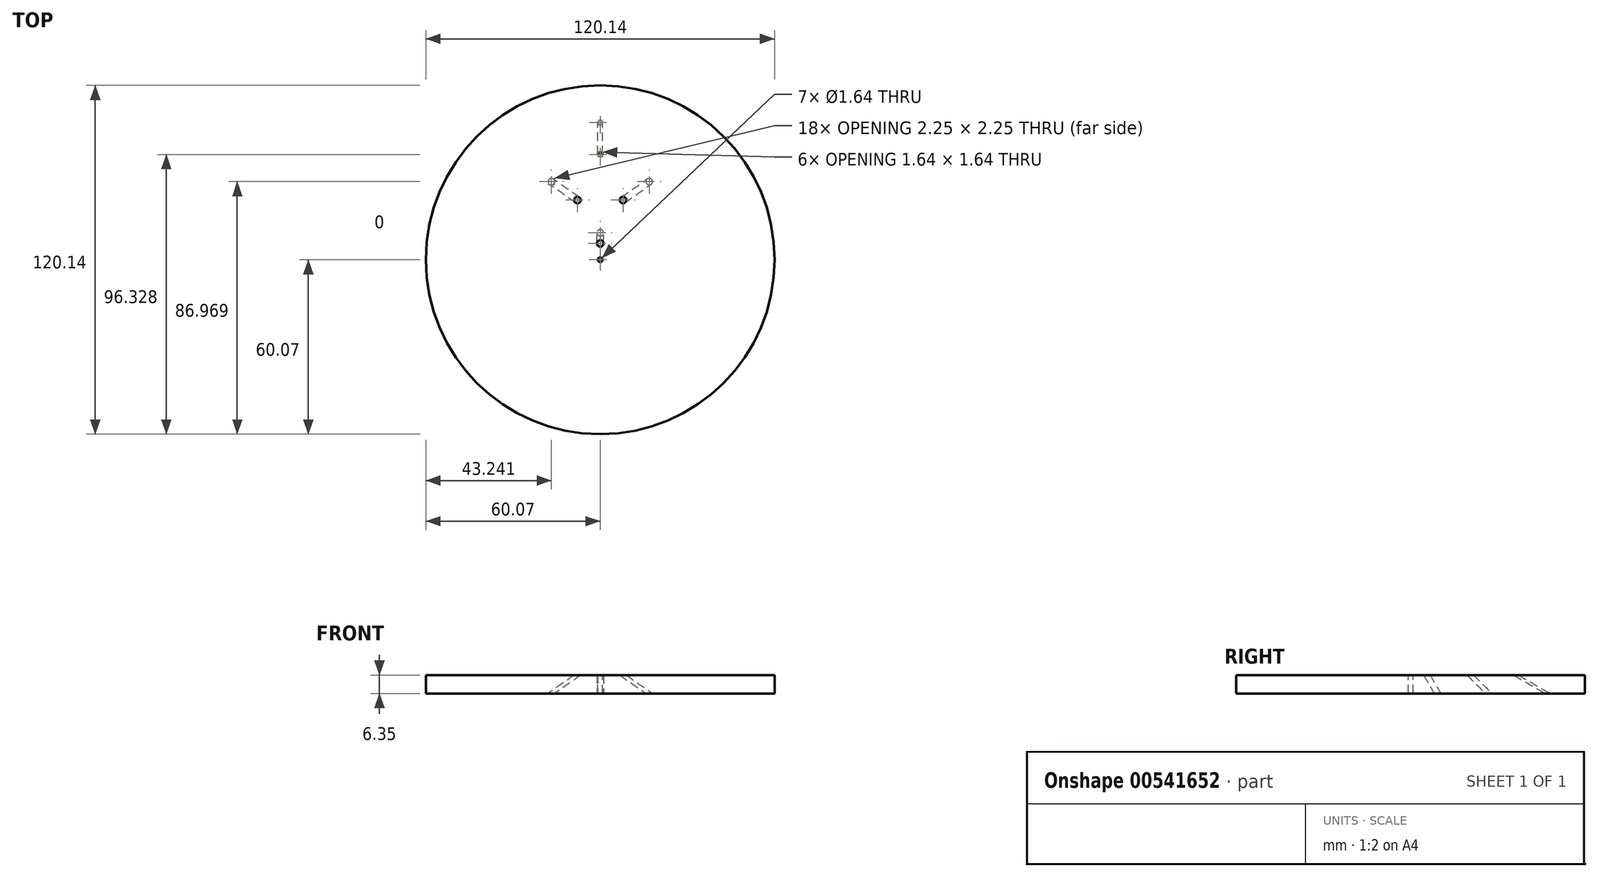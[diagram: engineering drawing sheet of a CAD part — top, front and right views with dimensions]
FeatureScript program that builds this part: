
annotation { "Feature Type Name" : "Feature", "Feature Type Description" : "" }
export const myFeature = defineFeature(function(context is Context, id is Id, definition is map)
    precondition{}
    {
        {
            var Q0;
            Q0=qCreatedBy(makeId("Top.planeOp"),FACE);
            var sketch = newSketch(context, id + "F0", { "sketchPlane" : qUnion([Q0])});
            skCircle(sketch, "E0", {"center": v(0, 0) * mm, "radius": 60.07 * mm});
            skSolve(sketch);
        }
        {
            var Q0;
            Q0=qCreatedBy(makeId("Top.planeOp"),FACE);
            var sketch = newSketch(context, id + "F1", { "sketchPlane" : qUnion([Q0])});
            skCircle(sketch, "E1", {"center": v(0, 0) * mm, "radius": 0.82 * mm});
            skCircle(sketch, "E2", {"center": v(0, 5.61) * mm, "radius": 1.12 * mm});
            skCircle(sketch, "E3", {"center": v(0, 36.26) * mm, "radius": 0.82 * mm});
            skCircle(sketch, "E4", {"center": v(-7.85, 20.55) * mm, "radius": 1.12 * mm});
            skCircle(sketch, "E5", {"center": v(7.85, 20.55) * mm, "radius": 1.12 * mm});
            skLineSegment(sketch, "E6", {"start": v(7.85, 20.55) * mm, "end": v(-7.85, 20.55) * mm, "construction": true});
            skSolve(sketch);
        }
        {
            var Q0;
            Q0=sQuery(id+"F1.wireOp",EDGE,"E6");
            cPlane(context, id + "F2", {"entities" : qUnion([Q0]), "cplaneType" : CPlaneType.LINE_ANGLE, "offset" : 25.4 * mm, "angle" : 45 * degree, "oppositeDirection" : true, "width" : 152.4 * mm, "height" : 152.4 * mm});
        }
        {
            var Q0;
            Q0=qCreatedBy(makeId("Top.planeOp"),FACE);
            var sketch = newSketch(context, id + "F3", { "sketchPlane" : qUnion([Q0])});
            skCircle(sketch, "E7.0", {"center": v(0, 0) * mm, "radius": 0.82 * mm});
            skSolve(sketch);
        }
        {
            var Q0;
            Q0=makeQuery(id+"F0.imprint","IMPRINT",FACE,{"disambiguationData":[TD([[makeQuery(id+"F0.imprint","IMPRINT",EDGE,{"derivedFrom":sQuery(id+"F0.wireOp",EDGE,"E0")}),1.0]])]});
            var sketch = newSketch(context, id + "F4", { "sketchPlane" : qUnion([Q0])});
            skCircle(sketch, "E8.0", {"center": v(0, 5.61) * mm, "radius": 1.12 * mm});
            skSolve(sketch);
        }
        {
            var Q0;
            Q0=qCreatedBy(makeId("Right.planeOp"),FACE);
            var sketch = newSketch(context, id + "F5", { "sketchPlane" : qUnion([Q0])});
            skLineSegment(sketch, "E9", {"start": v(5.61, 0) * mm, "end": v(-248.39, 439.94) * mm});
            skLineSegment(sketch, "E10", {"start": v(5.61, 0) * mm, "end": v(259.61, -439.94) * mm});
            skSolve(sketch);
        }
        {
            var Q0;
            Q0=qCreatedBy(makeId("Top.planeOp"),FACE);
            var sketch = newSketch(context, id + "F6", { "sketchPlane" : qUnion([Q0])});
            skCircle(sketch, "E11.0", {"center": v(7.85, 20.55) * mm, "radius": 1.12 * mm});
            skSolve(sketch);
        }
        {
            var Q0;
            Q0=qCreatedBy(id+"F2.planeOp",FACE);
            var sketch = newSketch(context, id + "F7", { "sketchPlane" : qUnion([Q0])});
            skLineSegment(sketch, "E12", {"start": v(7.85, -14.53) * mm, "end": v(-351.88, 344.16) * mm});
            skLineSegment(sketch, "E13", {"start": v(7.85, -14.53) * mm, "end": v(245.65, -251.64) * mm});
            skSolve(sketch);
        }
        {
            var Q0;
            Q0=qCreatedBy(makeId("Top.planeOp"),FACE);
            var sketch = newSketch(context, id + "F8", { "sketchPlane" : qUnion([Q0])});
            skCircle(sketch, "E14.0", {"center": v(-7.85, 20.55) * mm, "radius": 1.12 * mm});
            skSolve(sketch);
        }
        {
            var Q0;
            Q0=qCreatedBy(id+"F2.planeOp",FACE);
            var sketch = newSketch(context, id + "F9", { "sketchPlane" : qUnion([Q0])});
            skLineSegment(sketch, "E15", {"start": v(-7.85, -14.53) * mm, "end": v(351.36, 344.68) * mm});
            skLineSegment(sketch, "E16", {"start": v(-7.85, -14.53) * mm, "end": v(-367.06, -373.74) * mm});
            skSolve(sketch);
        }
        {
            var Q0;
            Q0=qCreatedBy(makeId("Top.planeOp"),FACE);
            var sketch = newSketch(context, id + "F10", { "sketchPlane" : qUnion([Q0])});
            skCircle(sketch, "E17.0", {"center": v(0, 36.26) * mm, "radius": 0.82 * mm});
            skSolve(sketch);
        }
        {
            var Q0;
            Q0=qCreatedBy(makeId("Right.planeOp"),FACE);
            var sketch = newSketch(context, id + "F11", { "sketchPlane" : qUnion([Q0])});
            skLineSegment(sketch, "E18", {"start": v(36.26, 0) * mm, "end": v(-403.68, 254) * mm});
            skLineSegment(sketch, "E19", {"start": v(36.26, 0) * mm, "end": v(476.2, -254) * mm});
            skSolve(sketch);
        }
        {
            var Q0;
            Q0=qSketchRegion(id+"F0",true);
            extrude(context, id + "F12", {"entities" : qUnion([Q0]), "oppositeDirection" : true, "depth" : 6.35 * mm, "offsetDistance" : 25.4 * mm});
        }
        {
            var Q0;
            Q0=qSketchRegion(id+"F3",true);
            extrude(context, id + "F13", {"entities" : qUnion([Q0]), "operationType" : NewBodyOperationType.REMOVE, "endBound" : BoundingType.THROUGH_ALL, "oppositeDirection" : true, "depth" : 25.4 * mm, "offsetDistance" : 25.4 * mm});
        }
        {
            var Q0;
            Q0=qSketchRegion(id+"F4",true);
            var Q1;
            Q1=sQuery(id+"F5.wireOp",EDGE,"E10");
            sweep(context, id + "F14", {"operationType" : NewBodyOperationType.REMOVE, "profiles" : qUnion([Q0]), "path" : qUnion([Q1])});
        }
        {
            var Q0;
            Q0=qSketchRegion(id+"F6",true);
            var Q1;
            Q1=sQuery(id+"F7.wireOp",EDGE,"E13");
            sweep(context, id + "F15", {"operationType" : NewBodyOperationType.REMOVE, "profiles" : qUnion([Q0]), "path" : qUnion([Q1])});
        }
        {
            var Q0;
            Q0=qSketchRegion(id+"F8",true);
            var Q1;
            Q1=sQuery(id+"F9.wireOp",EDGE,"E16");
            sweep(context, id + "F16", {"operationType" : NewBodyOperationType.REMOVE, "profiles" : qUnion([Q0]), "path" : qUnion([Q1])});
        }
        {
            var Q0;
            Q0=makeQuery(id+"F10.imprint","IMPRINT",FACE,{"disambiguationData":[TD([[makeQuery(id+"F10.imprint","IMPRINT",EDGE,{"derivedFrom":sQuery(id+"F10.wireOp",EDGE,"E17.0")}),1.0]])]});
            var Q1;
            Q1=sQuery(id+"F11.wireOp",EDGE,"E19");
            sweep(context, id + "F17", {"operationType" : NewBodyOperationType.REMOVE, "profiles" : qUnion([Q0]), "path" : qUnion([Q1])});
        }
    });
